# Revit family: TUBE GARDEN_JM6SW.1.24
name_source: partatom
category: Luminarias
units: mm (PartAtom-declared; Revit-internal decimal feet)

## family parameters
Compartido = No
Corte con vacíos al cargar = No
Cota de conector redondo = Diámetro de uso
Origen de luz = Sí
Punto de cálculo de habitación = No
Se basa en plano de trabajo = Sí
Siempre vertical = No
Tipo de pieza = Normal

## types (1)
- TUBE GARDEN_JM6SW.1.24
    Archivo de red fotométrica = JM6SW.1_24°.ies
    Cambio de temperatura de color de luz atenuada = <Ninguno>
    Comentarios de vataje = 100-240V
    Descripción = LUMINARIA DE JARDIN DIRIGIBLE CON DIFERENTES TIPOS DE SUJECION, CUERPO DE ALUMINIO FUNDIDO A PRESION CUBIERTO CON POLVO GRIS OSCURO Y VIDRIO TEMPLADO DE 4MM CON UN PESO DE 1KG, USO PARA INTERIORES Y EXTERIORES IP 66, 1 LED TIPO NICHIA CON UNA POTENCIA DE 7.4W, IRC 80, 593 LUMENES, TEMPERATURA EN BLANCO CALIDO 3000K, EFICIENCIA DE 79.63 LM/W, APERTURA DE 24 GRADOS POR STOCK, CABLE DE 1.9M H05RN-F, ALIMENTADO A 100-240V.
    Elevación por defecto = 0 mm  [stored 0 ft]
    Fabricante = BRILLANT
    Filtro de color = 16777215
    Lámpara = NICHIA
    Modelo = JM6SW.1.24
    Watt per fixture = 7.4
    Ángulo de inclinación = 60.00°

note: [stored X ft] marks values corroborated as IEEE doubles in the binary element streams (Revit-internal decimal feet)

## geometry (parser evidence)
native form markers: Blend x2
no freeform markers — native parametric forms only
